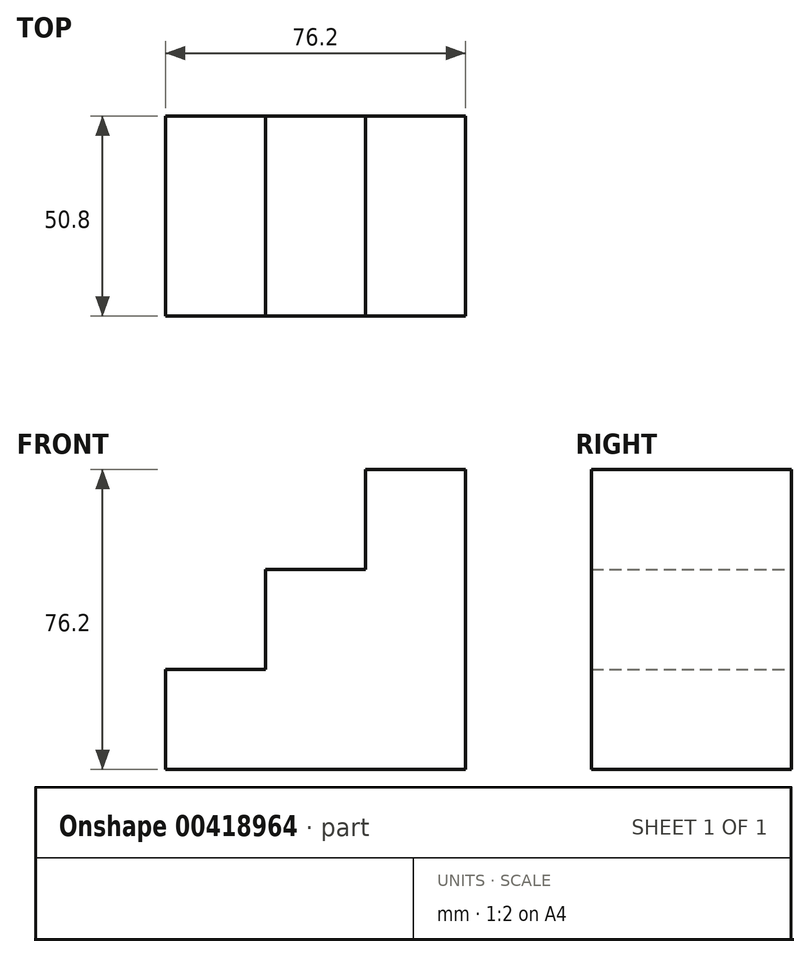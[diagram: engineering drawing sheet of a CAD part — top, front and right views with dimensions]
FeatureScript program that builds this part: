
annotation { "Feature Type Name" : "Feature", "Feature Type Description" : "" }
export const myFeature = defineFeature(function(context is Context, id is Id, definition is map)
    precondition{}
    {
        {
            var Q0;
            Q0=qCreatedBy(makeId("Front.planeOp"),FACE);
            var sketch = newSketch(context, id + "F0", { "sketchPlane" : qUnion([Q0])});
            skLineSegment(sketch, "E0", {"start": v(0, 0) * mm, "end": v(-76.2, 0) * mm});
            skLineSegment(sketch, "E1", {"start": v(-76.2, 0) * mm, "end": v(-76.2, 25.4) * mm});
            skLineSegment(sketch, "E2", {"start": v(-50.8, 25.4) * mm, "end": v(-76.2, 25.4) * mm});
            skLineSegment(sketch, "E3", {"start": v(-50.8, 50.8) * mm, "end": v(-50.8, 25.4) * mm});
            skLineSegment(sketch, "E4", {"start": v(-50.8, 50.8) * mm, "end": v(-25.4, 50.8) * mm});
            skLineSegment(sketch, "E5", {"start": v(-25.4, 50.8) * mm, "end": v(-25.4, 76.2) * mm});
            skLineSegment(sketch, "E6", {"start": v(-25.4, 76.2) * mm, "end": v(0, 76.2) * mm});
            skLineSegment(sketch, "E7", {"start": v(0, 0) * mm, "end": v(0, 76.2) * mm});
            skSolve(sketch);
        }
        {
            var Q0;
            Q0 = qSketchRegion(id + "F0", true);
            extrude(context, id + "F1", {"entities" : qUnion([Q0]), "depth" : 50.8 * mm});
        }
    });
